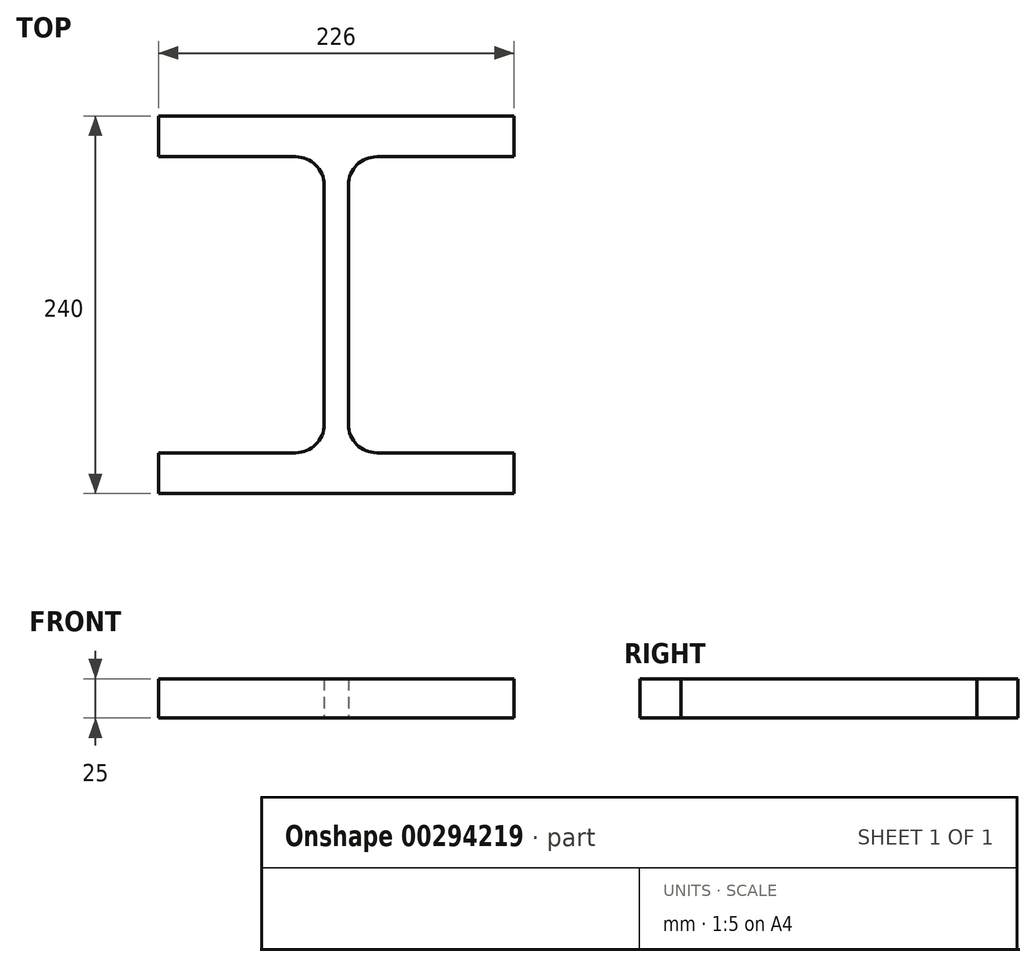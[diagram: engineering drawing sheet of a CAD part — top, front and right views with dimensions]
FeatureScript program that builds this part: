
annotation { "Feature Type Name" : "Feature", "Feature Type Description" : "" }
export const myFeature = defineFeature(function(context is Context, id is Id, definition is map)
    precondition{}
    {
        {
            var Q0;
            Q0=qCreatedBy(makeId("Top.planeOp"),FACE);
            var sketch = newSketch(context, id + "F0", { "sketchPlane" : qUnion([Q0])});
            skLineSegment(sketch, "E0", {"start": v(45.81, 176) * mm, "end": v(45.81, 24) * mm});
            skLineSegment(sketch, "E1", {"start": v(27.81, 6) * mm, "end": v(-59.44, 6) * mm});
            skLineSegment(sketch, "E2", {"start": v(-59.44, 6) * mm, "end": v(-59.44, -20) * mm});
            skLineSegment(sketch, "E3", {"start": v(-59.44, -20) * mm, "end": v(166.56, -20) * mm});
            skLineSegment(sketch, "E4", {"start": v(166.56, -20) * mm, "end": v(166.56, 6) * mm});
            skLineSegment(sketch, "E5", {"start": v(166.56, 6) * mm, "end": v(79.31, 6) * mm});
            skLineSegment(sketch, "E6", {"start": v(61.31, 24) * mm, "end": v(61.31, 176) * mm});
            skLineSegment(sketch, "E7", {"start": v(79.31, 194) * mm, "end": v(166.56, 194) * mm});
            skLineSegment(sketch, "E8", {"start": v(166.56, 194) * mm, "end": v(166.56, 220) * mm});
            skLineSegment(sketch, "E9", {"start": v(166.56, 220) * mm, "end": v(-59.44, 220) * mm});
            skLineSegment(sketch, "E10", {"start": v(-59.44, 220) * mm, "end": v(-59.44, 194) * mm});
            skLineSegment(sketch, "E11", {"start": v(-59.44, 194) * mm, "end": v(27.81, 194) * mm});
            skPoint(sketch, "E12.visualSharp", {"position": v(45.81, 194) * mm});
            skArc(sketch, "E12.filletArc", {"start": v(45.81, 176) * mm, "mid": v(40.54, 188.73) * mm, "end": v(27.81, 194) * mm});
            skPoint(sketch, "E13.visualSharp", {"position": v(61.31, 194) * mm});
            skArc(sketch, "E13.filletArc", {"start": v(79.31, 194) * mm, "mid": v(66.59, 188.73) * mm, "end": v(61.31, 176) * mm});
            skPoint(sketch, "E14.visualSharp", {"position": v(61.31, 6) * mm});
            skArc(sketch, "E14.filletArc", {"start": v(61.31, 24) * mm, "mid": v(66.59, 11.27) * mm, "end": v(79.31, 6) * mm});
            skPoint(sketch, "E15.visualSharp", {"position": v(45.81, 6) * mm});
            skArc(sketch, "E15.filletArc", {"start": v(27.81, 6) * mm, "mid": v(40.54, 11.27) * mm, "end": v(45.81, 24) * mm});
            skSolve(sketch);
        }
        {
            var Q0;
            Q0=makeQuery(id+"F0.imprint","IMPRINT",FACE,{"disambiguationData":[TD([[makeQuery(id+"F0.imprint","IMPRINT",EDGE,{"derivedFrom":sQuery(id+"F0.wireOp",EDGE,"E0")}),1.0]])]});
            extrude(context, id + "F1", {"entities" : qUnion([Q0]), "depth" : 25 * mm});
        }
    });
